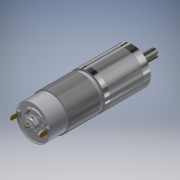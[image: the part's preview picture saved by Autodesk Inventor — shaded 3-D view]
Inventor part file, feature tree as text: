
AUTODESK INVENTOR PART (.ipt)
format: ipt  version: 2017.1 (Build 211199000, 199)  size: 367,616 bytes
history: native  units: in
note: dims shown in document units (in); Inventor stores cm internally (conversion verified against a paired STEP export)
features: mirror x1, other x1, imported_body x1
ambient origin geometry x8: Origin, YZ Plane, XZ Plane, XY Plane, X Axis, Y Axis, Z Axis, Center Point
bodies: Body1 (feature_tree)
feature tree (3):
  mirror  "Mirror2"
  other  "PG-71"
  imported_body  "Base1"
